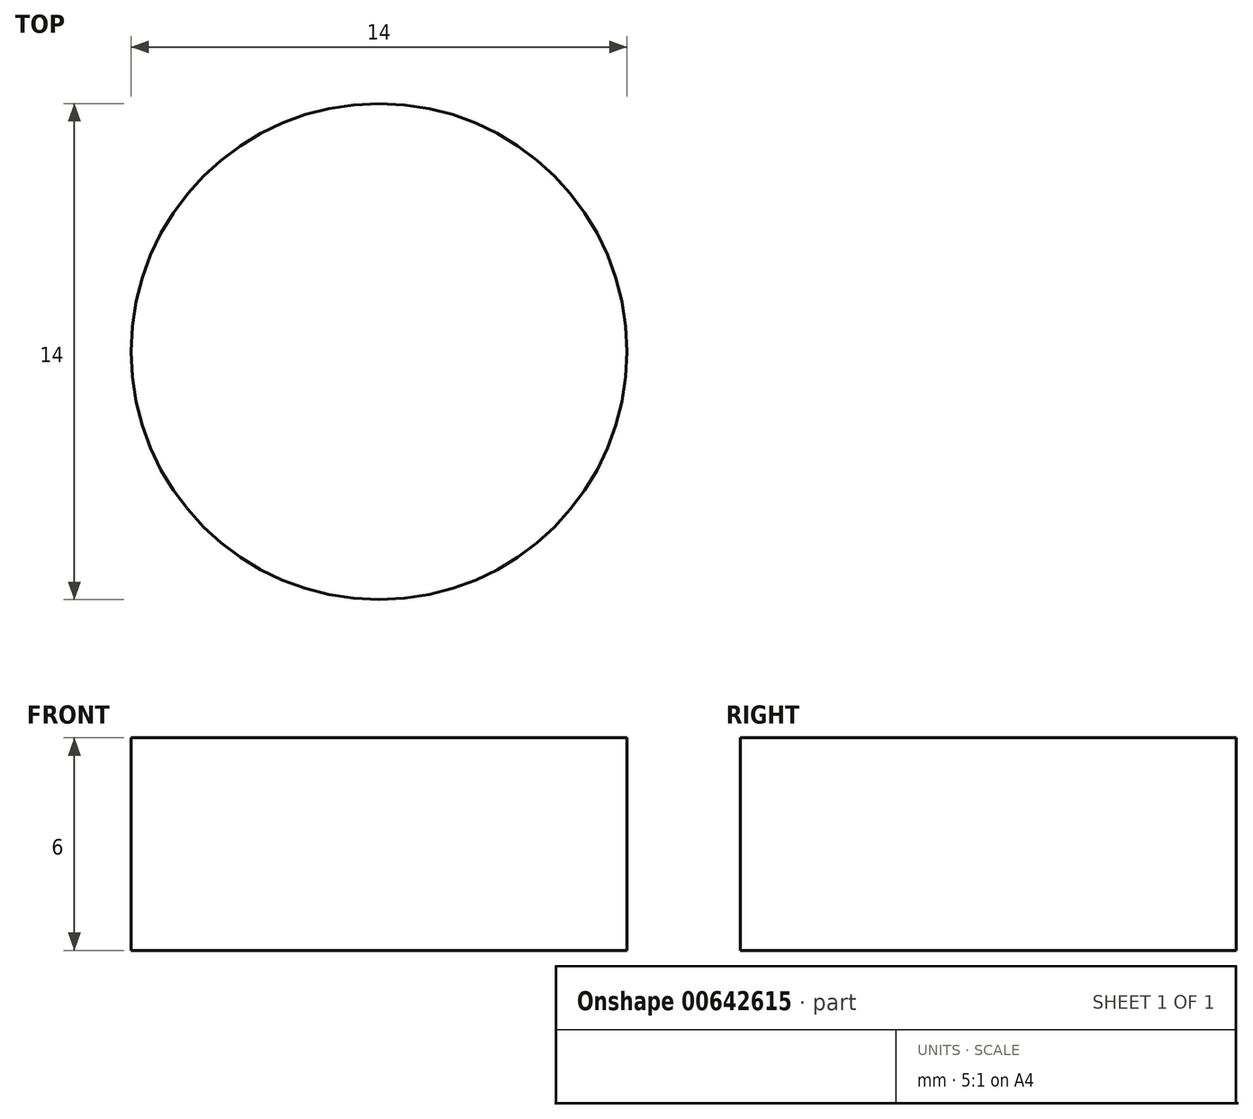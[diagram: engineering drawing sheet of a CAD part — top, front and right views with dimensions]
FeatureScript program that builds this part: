
annotation { "Feature Type Name" : "Feature", "Feature Type Description" : "" }
export const myFeature = defineFeature(function(context is Context, id is Id, definition is map)
    precondition{}
    {
        {
            var Q0;
            Q0=qCreatedBy(makeId("Top.planeOp"),FACE);
            var sketch = newSketch(context, id + "F0", { "sketchPlane" : qUnion([Q0])});
            skCircle(sketch, "E0", {"center": v(0, 0) * mm, "radius": 7 * mm});
            skSolve(sketch);
        }
        {
            var Q0;
            Q0 = qSketchRegion(id + "F0", true);
            extrude(context, id + "F1", {"entities" : qUnion([Q0]), "depth" : 6 * mm, "offsetDistance" : 25 * mm});
        }
    });
